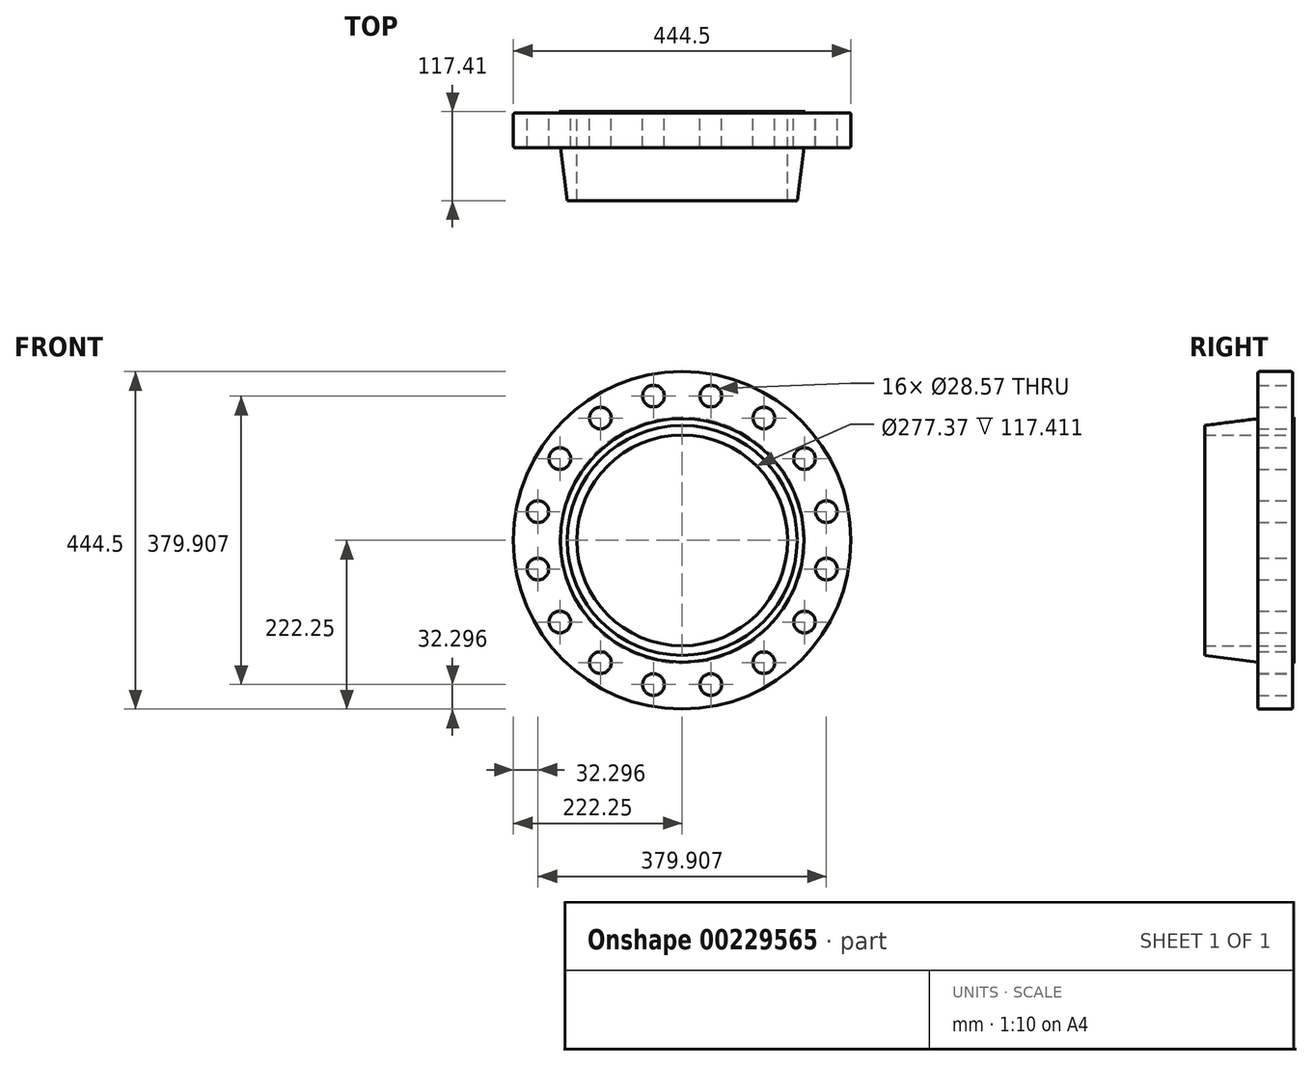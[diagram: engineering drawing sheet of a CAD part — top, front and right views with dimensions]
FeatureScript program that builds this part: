
annotation { "Feature Type Name" : "Feature", "Feature Type Description" : "" }
export const myFeature = defineFeature(function(context is Context, id is Id, definition is map)
    precondition{}
    {
        {
            var Q0;
            Q0=qCreatedBy(makeId("Front.planeOp"),FACE);
            var sketch = newSketch(context, id + "F0", { "sketchPlane" : qUnion([Q0])});
            skCircle(sketch, "E0", {"center": v(0, 0) * mm, "radius": 222.25 * mm});
            skCircle(sketch, "E1", {"center": v(0, 0) * mm, "radius": 136.53 * mm});
            skCircle(sketch, "E2", {"center": v(37.78, 189.95) * mm, "radius": 14.29 * mm});
            skCircle(sketch, "E3.1.0", {"center": v(-37.78, 189.95) * mm, "radius": 14.29 * mm});
            skCircle(sketch, "E3.2.0", {"center": v(-107.6, 161.03) * mm, "radius": 14.29 * mm});
            skCircle(sketch, "E3.3.0", {"center": v(-161.03, 107.6) * mm, "radius": 14.29 * mm});
            skCircle(sketch, "E3.4.0", {"center": v(-189.95, 37.78) * mm, "radius": 14.29 * mm});
            skCircle(sketch, "E3.5.0", {"center": v(-189.95, -37.78) * mm, "radius": 14.29 * mm});
            skCircle(sketch, "E3.6.0", {"center": v(-161.03, -107.6) * mm, "radius": 14.29 * mm});
            skCircle(sketch, "E3.7.0", {"center": v(-107.6, -161.03) * mm, "radius": 14.29 * mm});
            skCircle(sketch, "E3.8.0", {"center": v(-37.78, -189.95) * mm, "radius": 14.29 * mm});
            skCircle(sketch, "E3.9.0", {"center": v(37.78, -189.95) * mm, "radius": 14.29 * mm});
            skCircle(sketch, "E3.10.0", {"center": v(107.6, -161.03) * mm, "radius": 14.29 * mm});
            skCircle(sketch, "E3.11.0", {"center": v(161.03, -107.6) * mm, "radius": 14.29 * mm});
            skCircle(sketch, "E3.12.0", {"center": v(189.95, -37.78) * mm, "radius": 14.29 * mm});
            skCircle(sketch, "E3.13.0", {"center": v(189.95, 37.78) * mm, "radius": 14.29 * mm});
            skCircle(sketch, "E3.14.0", {"center": v(161.03, 107.6) * mm, "radius": 14.29 * mm});
            skCircle(sketch, "E3.15.0", {"center": v(107.6, 161.03) * mm, "radius": 14.29 * mm});
            skSolve(sketch);
        }
        {
            var Q0;
            Q0 = qSketchRegion(id + "F0", true);
            extrude(context, id + "F1", {"entities" : qUnion([Q0]), "depth" : 45.97 * mm});
        }
        {
            var Q0;
            Q0=qCreatedBy(makeId("Right.planeOp"),FACE);
            var sketch = newSketch(context, id + "F2", { "sketchPlane" : qUnion([Q0])});
            skLineSegment(sketch, "E4", {"start": v(0, 0) * mm, "end": v(-122.17, 0) * mm});
            skLineSegment(sketch, "E5", {"start": v(-45.97, 0) * mm, "end": v(-45.97, 160.27) * mm});
            skLineSegment(sketch, "E6", {"start": v(0, 0) * mm, "end": v(0, 138.68) * mm});
            skLineSegment(sketch, "E7", {"start": v(0, 138.68) * mm, "end": v(-115.82, 138.68) * mm});
            skLineSegment(sketch, "E8", {"start": v(-45.97, 160.27) * mm, "end": v(0, 160.27) * mm});
            skLineSegment(sketch, "E9", {"start": v(0, 160.27) * mm, "end": v(0, 138.68) * mm});
            skLineSegment(sketch, "E10", {"start": v(-115.82, 138.68) * mm, "end": v(-115.82, 151.32) * mm});
            skLineSegment(sketch, "E11", {"start": v(-115.82, 151.32) * mm, "end": v(-45.97, 160.27) * mm});
            skSolve(sketch);
        }
        {
            var Q0;
            Q0 = qSketchRegion(id + "F2", true);
            var Q1;
            Q1=sQuery(id+"F2.wireOp",EDGE,"E4");
            revolve(context, id + "F3", {"operationType" : NewBodyOperationType.ADD, "entities" : qUnion([Q0]), "axis" : qUnion([Q1]), "revolveType" : RevolveType.FULL});
        }
        {
            var Q0;
            Q0=makeQuery(id+"F3.boolean.opBoolean","MERGE",FACE,{"derivedFrom":[makeQuery(id+"F1.opExtrude","CAP_FACE",FACE,{"disambiguationData":[OSD([sQuery(id+"F0.wireOp",EDGE,"E0"),sQuery(id+"F0.wireOp",EDGE,"E1"),sQuery(id+"F0.wireOp",EDGE,"E2"),sQuery(id+"F0.wireOp",EDGE,"E3.1.0"),sQuery(id+"F0.wireOp",EDGE,"E3.2.0"),sQuery(id+"F0.wireOp",EDGE,"E3.3.0"),sQuery(id+"F0.wireOp",EDGE,"E3.4.0"),sQuery(id+"F0.wireOp",EDGE,"E3.5.0"),sQuery(id+"F0.wireOp",EDGE,"E3.6.0"),sQuery(id+"F0.wireOp",EDGE,"E3.7.0"),sQuery(id+"F0.wireOp",EDGE,"E3.8.0"),sQuery(id+"F0.wireOp",EDGE,"E3.9.0"),sQuery(id+"F0.wireOp",EDGE,"E3.10.0"),sQuery(id+"F0.wireOp",EDGE,"E3.11.0"),sQuery(id+"F0.wireOp",EDGE,"E3.12.0"),sQuery(id+"F0.wireOp",EDGE,"E3.13.0"),sQuery(id+"F0.wireOp",EDGE,"E3.14.0"),sQuery(id+"F0.wireOp",EDGE,"E3.15.0")])],"isStart":true}),makeQuery(id+"F3.opRevolve","SWEPT_FACE",FACE,{"disambiguationData":[OSD([sQuery(id+"F2.wireOp",EDGE,"E6"),sQuery(id+"F2.wireOp",EDGE,"E9")])]})]});
            var sketch = newSketch(context, id + "F4", { "sketchPlane" : qUnion([Q0])});
            skCircle(sketch, "E12", {"center": v(0, 0) * mm, "radius": 138.68 * mm});
            skSolve(sketch);
        }
        {
            var Q0;
            Q0 = qSketchRegion(id + "F4", true);
            extrude(context, id + "F5", {"entities" : qUnion([Q0]), "operationType" : NewBodyOperationType.REMOVE, "endBound" : BoundingType.THROUGH_ALL, "oppositeDirection" : true, "depth" : 25.4 * mm});
        }
        {
            var Q0;
            Q0=makeQuery(id+"F3.boolean.opBoolean","MERGE",FACE,{"derivedFrom":[makeQuery(id+"F1.opExtrude","CAP_FACE",FACE,{"disambiguationData":[OSD([sQuery(id+"F0.wireOp",EDGE,"E0"),sQuery(id+"F0.wireOp",EDGE,"E1"),sQuery(id+"F0.wireOp",EDGE,"E2"),sQuery(id+"F0.wireOp",EDGE,"E3.1.0"),sQuery(id+"F0.wireOp",EDGE,"E3.2.0"),sQuery(id+"F0.wireOp",EDGE,"E3.3.0"),sQuery(id+"F0.wireOp",EDGE,"E3.4.0"),sQuery(id+"F0.wireOp",EDGE,"E3.5.0"),sQuery(id+"F0.wireOp",EDGE,"E3.6.0"),sQuery(id+"F0.wireOp",EDGE,"E3.7.0"),sQuery(id+"F0.wireOp",EDGE,"E3.8.0"),sQuery(id+"F0.wireOp",EDGE,"E3.9.0"),sQuery(id+"F0.wireOp",EDGE,"E3.10.0"),sQuery(id+"F0.wireOp",EDGE,"E3.11.0"),sQuery(id+"F0.wireOp",EDGE,"E3.12.0"),sQuery(id+"F0.wireOp",EDGE,"E3.13.0"),sQuery(id+"F0.wireOp",EDGE,"E3.14.0"),sQuery(id+"F0.wireOp",EDGE,"E3.15.0")])],"isStart":true}),makeQuery(id+"F3.opRevolve","SWEPT_FACE",FACE,{"disambiguationData":[OSD([sQuery(id+"F2.wireOp",EDGE,"E6"),sQuery(id+"F2.wireOp",EDGE,"E9")])]})]});
            var sketch = newSketch(context, id + "F6", { "sketchPlane" : qUnion([Q0])});
            skCircle(sketch, "E13", {"center": v(0, 0) * mm, "radius": 127.25 * mm});
            skCircle(sketch, "E14", {"center": v(0, 0) * mm, "radius": 161.93 * mm});
            skSolve(sketch);
        }
        {
            var Q0;
            Q0 = qSketchRegion(id + "F6", true);
            extrude(context, id + "F7", {"entities" : qUnion([Q0]), "operationType" : NewBodyOperationType.ADD, "depth" : 1.59 * mm});
        }
        {
            var Q0;
            Q0=makeQuery(id+"F1.opExtrude","CAP_EDGE",EDGE,{"disambiguationData":[OSD([sQuery(id+"F0.wireOp",EDGE,"E0")])],"isStart":true});
            var Q1;
            Q1=makeQuery(id+"F1.opExtrude","CAP_EDGE",EDGE,{"disambiguationData":[OSD([sQuery(id+"F0.wireOp",EDGE,"E0")])],"isStart":false});
            var Q2;
            Q2=makeQuery(id+"F3.opRevolve","SWEPT_EDGE",EDGE,{"disambiguationData":[OSD([sQuery(id+"F2.wireOp",EDGE,"E5"),sQuery(id+"F2.wireOp",EDGE,"E8"),sQuery(id+"F2.wireOp",EDGE,"JVtbjjuH-dZmT-9VTl-TT2N-Bfg4vhyALmHo")])]});
            fillet(context, id + "F8", {"entities" : qUnion([Q0, Q1, Q2]), "radius" : 2.54 * mm, "tangentPropagation" : true, "allowEdgeOverflow" : false});
        }
        {
            var Q0;
            Q0=makeQuery(id+"F7.opExtrude","CAP_FACE",FACE,{"disambiguationData":[OSD([sQuery(id+"F6.wireOp",EDGE,"E13"),sQuery(id+"F6.wireOp",EDGE,"E14")])],"isStart":true});
            extrude(context, id + "F9", {"entities" : qUnion([Q0]), "operationType" : NewBodyOperationType.REMOVE, "oppositeDirection" : true, "depth" : 25.4 * mm});
        }
    });
